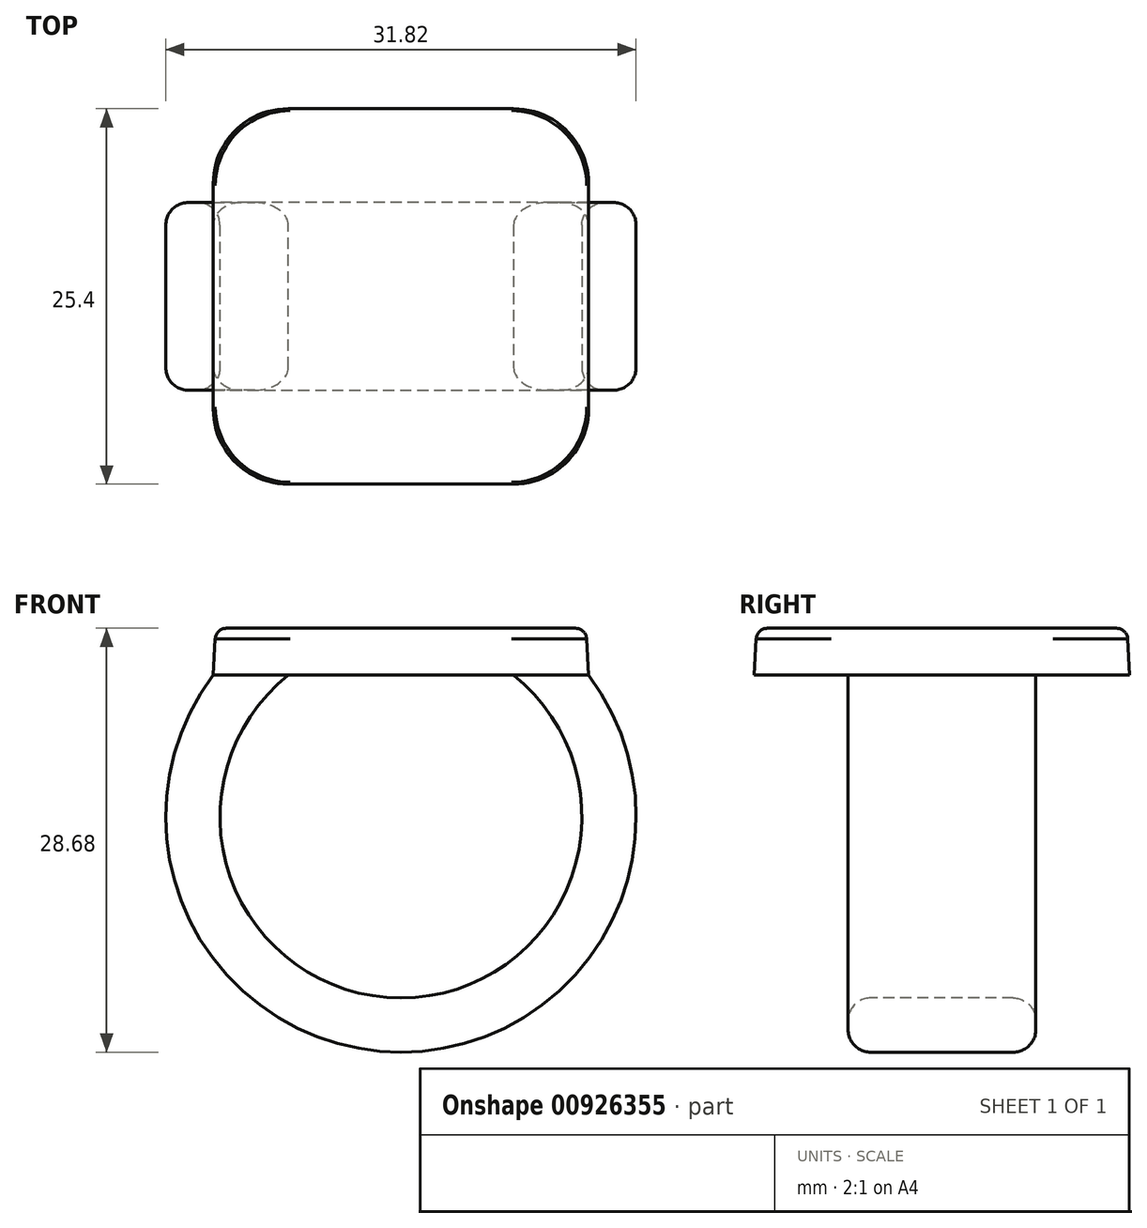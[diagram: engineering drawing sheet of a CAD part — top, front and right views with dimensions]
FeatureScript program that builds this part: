
annotation { "Feature Type Name" : "Feature", "Feature Type Description" : "" }
export const myFeature = defineFeature(function(context is Context, id is Id, definition is map)
    precondition{}
    {
        {
            var Q0;
            Q0=qCreatedBy(makeId("Top.planeOp"),FACE);
            var sketch = newSketch(context, id + "F0", { "sketchPlane" : qUnion([Q0])});
            skLineSegment(sketch, "E0.bottom", {"start": v(-12.7, 12.7) * mm, "end": v(12.7, 12.7) * mm});
            skLineSegment(sketch, "E0.top", {"start": v(-12.7, -12.7) * mm, "end": v(12.7, -12.7) * mm});
            skLineSegment(sketch, "E0.left", {"start": v(-12.7, 12.7) * mm, "end": v(-12.7, -12.7) * mm});
            skLineSegment(sketch, "E0.right", {"start": v(12.7, 12.7) * mm, "end": v(12.7, -12.7) * mm});
            skPoint(sketch, "E0.middle", {"position": v(0, 0) * mm});
            skSolve(sketch);
        }
        {
            var Q0;
            Q0=makeQuery(id+"F0.imprint","IMPRINT",FACE,{"disambiguationData":[TD([[makeQuery(id+"F0.imprint","IMPRINT",EDGE,{"derivedFrom":sQuery(id+"F0.wireOp",EDGE,"E0.bottom")}),-1.0]])]});
            extrude(context, id + "F1", {"entities" : qUnion([Q0]), "depth" : 3.17 * mm, "offsetDistance" : 25.4 * mm, "hasDraft" : true, "draftAngle" : 3 * degree, "draftPullDirection" : true});
        }
        {
            var Q0;
            Q0=qCreatedBy(makeId("Front.planeOp"),FACE);
            var sketch = newSketch(context, id + "F2", { "sketchPlane" : qUnion([Q0])});
            skArc(sketch, "E1", {"start": v(-10.16, 0) * mm, "mid": v(0, -23.56) * mm, "end": v(10.16, 0) * mm});
            skSolve(sketch);
        }
        {
            var Q0;
            Q0=qCreatedBy(makeId("Top.planeOp"),FACE);
            var sketch = newSketch(context, id + "F3", { "sketchPlane" : qUnion([Q0])});
            skPoint(sketch, "E2.middle", {"position": v(-1.66, 0) * mm});
            skLineSegment(sketch, "E3.0", {"start": v(13.97, 0) * mm, "end": v(-13.97, 0) * mm});
            skPoint(sketch, "E4.0", {"position": v(-10.16, 0) * mm});
            skLineSegment(sketch, "E5.bottom", {"start": v(-7.62, -6.35) * mm, "end": v(-12.7, -6.35) * mm});
            skLineSegment(sketch, "E5.top", {"start": v(-7.62, 6.35) * mm, "end": v(-12.7, 6.35) * mm});
            skLineSegment(sketch, "E5.left", {"start": v(-7.62, -6.35) * mm, "end": v(-7.62, 6.35) * mm});
            skLineSegment(sketch, "E5.right", {"start": v(-12.7, -6.35) * mm, "end": v(-12.7, 6.35) * mm});
            skSolve(sketch);
        }
        {
            var Q0;
            Q0 = qSketchRegion(id + "F3", true);
            var Q1;
            Q1 = qConstructionFilter(qBodyType(qCreatedBy(id + "F2" ,EDGE), BodyType.WIRE), ConstructionObject.NO);
            sweep(context, id + "F4", {"operationType" : NewBodyOperationType.ADD, "profiles" : qUnion([Q0]), "path" : qUnion([Q1])});
        }
        {
            var Q0;
            Q0=makeQuery(id+"F4.opSweep","SWEPT_FACE",FACE,{"disambiguationData":[OSD([sQuery(id+"F2.wireOp",EDGE,"E1"),sQuery(id+"F3.wireOp",EDGE,"E5.bottom")])]});
            var sketch = newSketch(context, id + "F5", { "sketchPlane" : qUnion([Q0])});
            skArc(sketch, "E6.0", {"start": v(-7.62, 0) * mm, "mid": v(0, -21.84) * mm, "end": v(7.62, 0) * mm});
            skLineSegment(sketch, "E6.2", {"start": v(-12.7, 0) * mm, "end": v(-7.62, 0) * mm});
            skPoint(sketch, "E7.orphan", {"position": v(10.01, -2.54) * mm});
            skPoint(sketch, "E6.1.end.orphan", {"position": v(10.16, 0) * mm});
            skLineSegment(sketch, "E8.trimOffspring", {"start": v(7.62, 0) * mm, "end": v(12.7, 0) * mm});
            skSolve(sketch);
        }
        {
            var Q0;
            {var subQ1=makeQuery(id+"F4.opSweep","CAP_EDGE",EDGE,{"disambiguationData":[OSD([sQuery(id+"F2.wireOp",VERTEX,"E1.end"),sQuery(id+"F3.wireOp",EDGE,"E5.bottom")])],"isStart":false});Q0=makeQuery(id+"F5.imprint","IMPRINT",FACE,{"disambiguationData":[TD([[makeQuery(id+"F5.imprint","IMPRINT",EDGE,{"derivedFrom":subQ1}),1.0]])]});}
            var Q1;
            Q1=makeQuery(id+"F4.opSweep","SWEPT_FACE",FACE,{"disambiguationData":[OSD([sQuery(id+"F2.wireOp",EDGE,"E1"),sQuery(id+"F3.wireOp",EDGE,"E5.top")])]});
            extrude(context, id + "F6", {"entities" : qUnion([Q0]), "operationType" : NewBodyOperationType.ADD, "endBound" : BoundingType.UP_TO_SURFACE, "oppositeDirection" : true, "depth" : 25.4 * mm, "endBoundEntityFace" : qUnion([Q1]), "offsetDistance" : 25.4 * mm});
        }
        {
            var Q0;
            Q0=makeQuery(id+"F1.opExtrude","SWEPT_EDGE",EDGE,{"disambiguationData":[OSD([sQuery(id+"F0.wireOp",EDGE,"E0.bottom"),sQuery(id+"F0.wireOp",EDGE,"E0.right")])]});
            var Q1;
            Q1=makeQuery(id+"F1.opExtrude","SWEPT_EDGE",EDGE,{"disambiguationData":[OSD([sQuery(id+"F0.wireOp",EDGE,"E0.bottom"),sQuery(id+"F0.wireOp",EDGE,"E0.left")])]});
            var Q2;
            Q2=makeQuery(id+"F1.opExtrude","SWEPT_EDGE",EDGE,{"disambiguationData":[OSD([sQuery(id+"F0.wireOp",EDGE,"E0.top"),sQuery(id+"F0.wireOp",EDGE,"E0.right")])]});
            var Q3;
            Q3=makeQuery(id+"F1.opExtrude","SWEPT_EDGE",EDGE,{"disambiguationData":[OSD([sQuery(id+"F0.wireOp",EDGE,"E0.top"),sQuery(id+"F0.wireOp",EDGE,"E0.left")])]});
            fillet(context, id + "F7", {"entities" : qUnion([Q0, Q1, Q2, Q3]), "radius" : 5.08 * mm, "tangentPropagation" : true, "allowEdgeOverflow" : false});
        }
        {
            var Q0;
            Q0=makeQuery(id+"F6.boolean.opBoolean","MERGE",EDGE,{"derivedFrom":[makeQuery(id+"F4.opSweep","SWEPT_EDGE",EDGE,{"disambiguationData":[OSD([sQuery(id+"F2.wireOp",EDGE,"E1"),sQuery(id+"F3.wireOp",EDGE,"E5.bottom"),sQuery(id+"F3.wireOp",EDGE,"E5.left")])]}),makeQuery(id+"F6.opExtrude","CAP_EDGE",EDGE,{"disambiguationData":[OSD([sQuery(id+"F5.wireOp",EDGE,"E6.0")])],"isStart":true})]});
            var Q1;
            Q1=makeQuery(id+"F4.opSweep","SWEPT_EDGE",EDGE,{"disambiguationData":[OSD([sQuery(id+"F2.wireOp",EDGE,"E1"),sQuery(id+"F3.wireOp",EDGE,"E5.bottom"),sQuery(id+"F3.wireOp",EDGE,"E5.right")])]});
            var Q2;
            Q2=makeQuery(id+"F4.opSweep","SWEPT_EDGE",EDGE,{"disambiguationData":[OSD([sQuery(id+"F2.wireOp",EDGE,"E1"),sQuery(id+"F3.wireOp",EDGE,"E5.top"),sQuery(id+"F3.wireOp",EDGE,"E5.right")])]});
            var Q3;
            Q3=makeQuery(id+"F6.boolean.opBoolean","MERGE",EDGE,{"derivedFrom":[makeQuery(id+"F4.opSweep","SWEPT_EDGE",EDGE,{"disambiguationData":[OSD([sQuery(id+"F2.wireOp",EDGE,"E1"),sQuery(id+"F3.wireOp",EDGE,"E5.top"),sQuery(id+"F3.wireOp",EDGE,"E5.left")])]}),makeQuery(id+"F6.opExtrude","CAP_EDGE",EDGE,{"disambiguationData":[OSD([sQuery(id+"F5.wireOp",EDGE,"E6.0")])],"isStart":false})]});
            fillet(context, id + "F8", {"entities" : qUnion([Q0, Q1, Q2, Q3]), "radius" : 1.52 * mm, "tangentPropagation" : true, "allowEdgeOverflow" : false});
        }
        {
            var Q0;
            Q0=makeQuery(id+"F1.opExtrude","CAP_FACE",FACE,{"disambiguationData":[OSD([sQuery(id+"F0.wireOp",EDGE,"E0.bottom"),sQuery(id+"F0.wireOp",EDGE,"E0.top"),sQuery(id+"F0.wireOp",EDGE,"E0.left"),sQuery(id+"F0.wireOp",EDGE,"E0.right")])],"isStart":false});
            fillet(context, id + "F9", {"entities" : qUnion([Q0]), "radius" : 0.76 * mm, "tangentPropagation" : true, "allowEdgeOverflow" : false});
        }
    });
